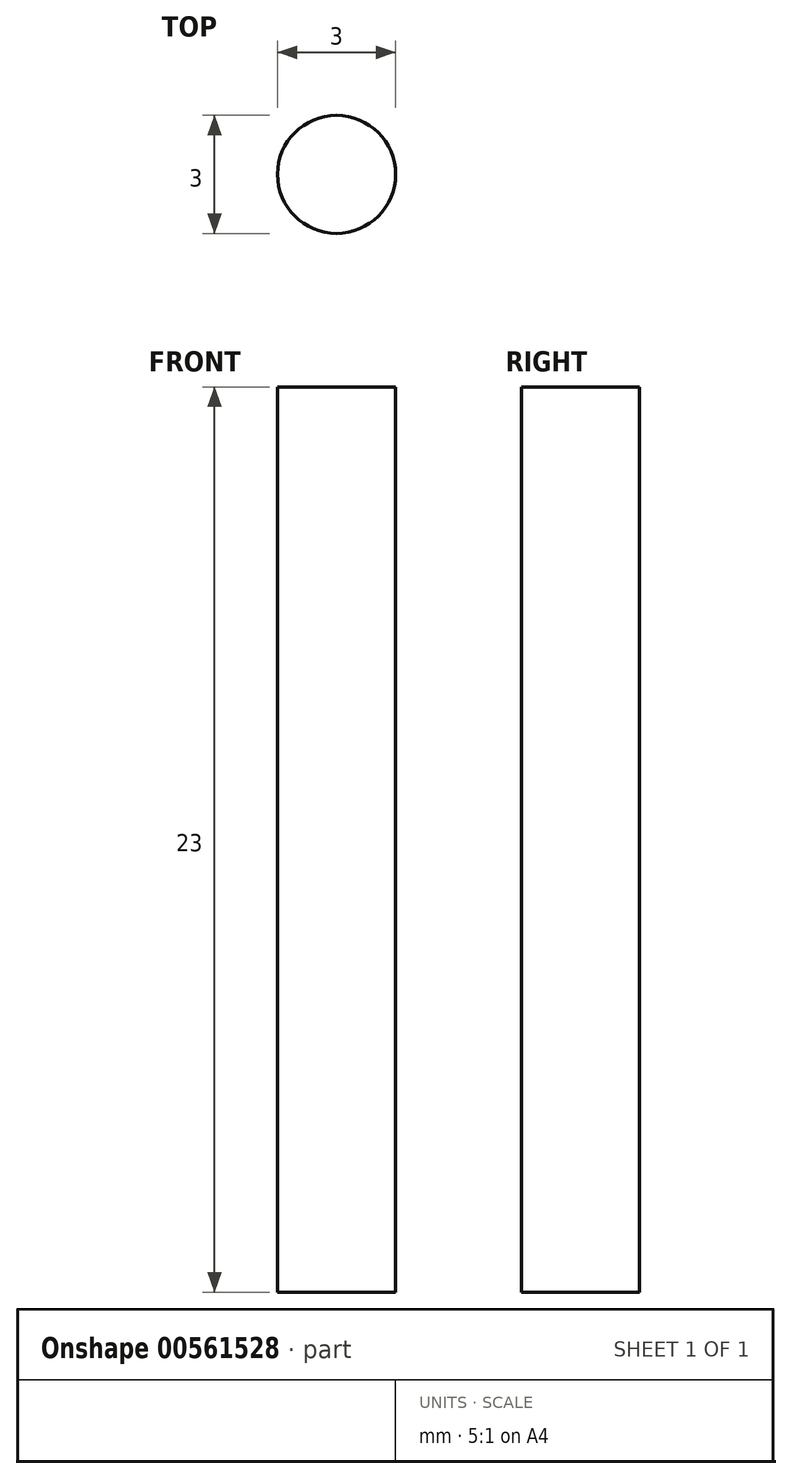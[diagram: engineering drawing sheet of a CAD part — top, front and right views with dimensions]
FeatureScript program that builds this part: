
annotation { "Feature Type Name" : "Feature", "Feature Type Description" : "" }
export const myFeature = defineFeature(function(context is Context, id is Id, definition is map)
    precondition{}
    {
        {
            var Q0;
            Q0=qCreatedBy(makeId("Top.planeOp"),FACE);
            var sketch = newSketch(context, id + "F0", { "sketchPlane" : qUnion([Q0])});
            skCircle(sketch, "E0", {"center": v(0, 0) * mm, "radius": 1.5 * mm});
            skSolve(sketch);
        }
        {
            var Q0;
            Q0 = qSketchRegion(id + "F0", true);
            extrude(context, id + "F1", {"entities" : qUnion([Q0]), "depth" : 23 * mm, "offsetDistance" : 25 * mm, "symmetric" : true});
        }
    });
